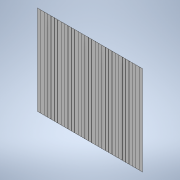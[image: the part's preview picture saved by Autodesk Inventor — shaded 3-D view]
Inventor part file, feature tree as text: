
AUTODESK INVENTOR PART (.ipt)
format: ipt  version: 2021 (Build 250183000, 183)  size: 482,304 bytes
history: native  units: in
note: dims shown in document units (in); Inventor stores cm internally (conversion verified against a paired STEP export)
features: extrude x3, sketch x3, pattern_linear x1, projected_geometry x1
ambient origin geometry x8: Origin, YZ Plane, XZ Plane, XY Plane, X Axis, Y Axis, Z Axis, Center Point
bodies: Solid1 (feature_tree)
feature tree (8):
  extrude  "Extrusion1"  Depth=2.742in
  extrude  "Extrusion2"  Depth=0.1in
  pattern_linear  "Rectangular Pattern1"  Count1=31 Spacing1=0.104in
  extrude  "Extrusion3"  Depth=0.104in TaperAngle=0.0deg
  sketch  "Sketch1"  dims[d0=4.0in d1=2.742in]
  sketch  "Sketch2"  dims[d2=0.04in d3=0.0in d4=0.1in]
  projected_geometry  "Projected Loop1"
  sketch  "Sketch3"  dims[d5=0.0015in d6=0.0in d7=12.2047in d9=0.104in d10=1.0in d11=0.0in]
